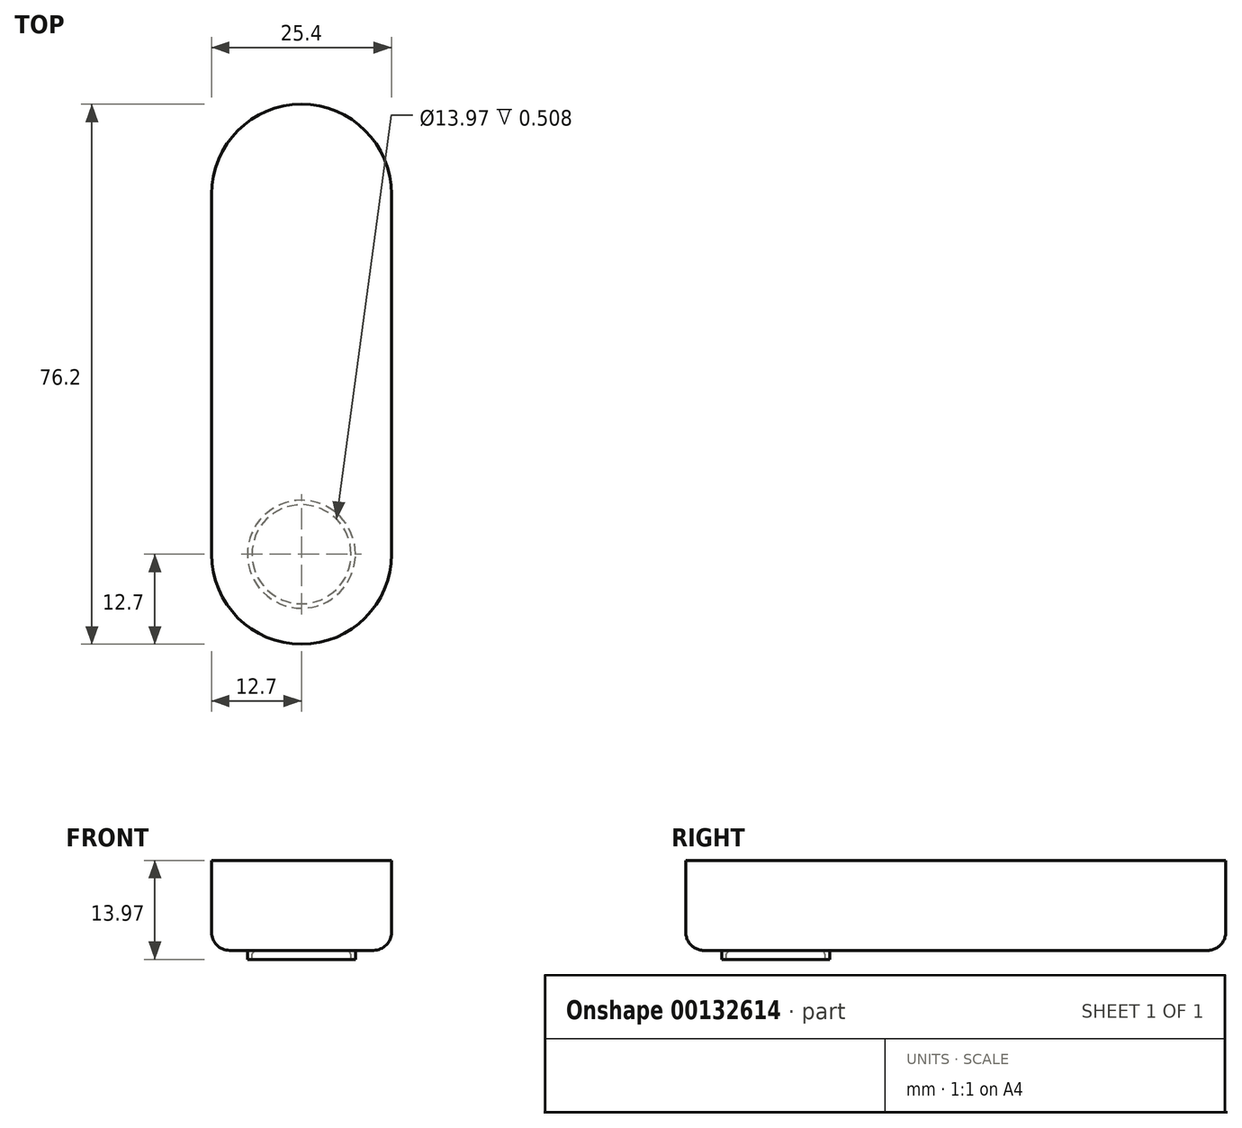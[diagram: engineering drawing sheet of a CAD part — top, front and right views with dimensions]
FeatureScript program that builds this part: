
annotation { "Feature Type Name" : "Feature", "Feature Type Description" : "" }
export const myFeature = defineFeature(function(context is Context, id is Id, definition is map)
    precondition{}
    {
        {
            var Q0;
            Q0=qCreatedBy(makeId("Top.planeOp"),FACE);
            var sketch = newSketch(context, id + "F0", { "sketchPlane" : qUnion([Q0])});
            skLineSegment(sketch, "E0.bottom", {"start": v(50.8, -50.8) * mm, "end": v(-50.8, -50.8) * mm});
            skLineSegment(sketch, "E0.top", {"start": v(50.8, 50.8) * mm, "end": v(-50.8, 50.8) * mm});
            skLineSegment(sketch, "E0.left", {"start": v(50.8, -50.8) * mm, "end": v(50.8, 50.8) * mm});
            skLineSegment(sketch, "E0.right", {"start": v(-50.8, -50.8) * mm, "end": v(-50.8, 50.8) * mm});
            skPoint(sketch, "E0.middle", {"position": v(0, 0) * mm});
            skSolve(sketch);
        }
        {
            var Q0;
            Q0=makeQuery(id+"F0.imprint","IMPRINT",FACE,{"disambiguationData":[TD([[makeQuery(id+"F0.imprint","IMPRINT",EDGE,{"derivedFrom":sQuery(id+"F0.wireOp",EDGE,"E0.bottom")}),-1.0]])]});
            extrude(context, id + "F1", {"entities" : qUnion([Q0]), "depth" : 50.8 * mm});
        }
        {
            var Q0;
            Q0=makeQuery(id+"F1.opExtrude","CAP_FACE",FACE,{"disambiguationData":[OSD([sQuery(id+"F0.wireOp",EDGE,"E0.bottom"),sQuery(id+"F0.wireOp",EDGE,"E0.top"),sQuery(id+"F0.wireOp",EDGE,"E0.left"),sQuery(id+"F0.wireOp",EDGE,"E0.right")])],"isStart":false});
            var sketch = newSketch(context, id + "F2", { "sketchPlane" : qUnion([Q0])});
            skLineSegment(sketch, "E1.bottom", {"start": v(12.7, -25.4) * mm, "end": v(-12.7, -25.4) * mm});
            skLineSegment(sketch, "E1.top", {"start": v(12.7, 25.4) * mm, "end": v(-12.7, 25.4) * mm});
            skLineSegment(sketch, "E1.left", {"start": v(12.7, -25.4) * mm, "end": v(12.7, 25.4) * mm});
            skLineSegment(sketch, "E1.right", {"start": v(-12.7, -25.4) * mm, "end": v(-12.7, 25.4) * mm});
            skPoint(sketch, "E1.middle", {"position": v(0, 0) * mm});
            skCircle(sketch, "E2", {"center": v(0, 25.4) * mm, "radius": 12.7 * mm});
            skCircle(sketch, "E3", {"center": v(0, -25.4) * mm, "radius": 12.7 * mm});
            skSolve(sketch);
        }
        {
            var Q0;
            {var subQ0=sQuery(id+"F2.wireOp",EDGE,"E1.top");Q0=makeQuery(id+"F2.imprint","IMPRINT",FACE,{"disambiguationData":[TD([[makeQuery(id+"F2.imprint","IMPRINT",EDGE,{"derivedFrom":subQ0}),-1.0]])]});}
            var Q1;
            {var subQ0=sQuery(id+"F2.wireOp",EDGE,"E1.top");Q1=makeQuery(id+"F2.imprint","IMPRINT",FACE,{"disambiguationData":[TD([[makeQuery(id+"F2.imprint","IMPRINT",EDGE,{"derivedFrom":subQ0}),1.0]])]});}
            var Q2;
            {var subQ0=sQuery(id+"F2.wireOp",EDGE,"E1.left");Q2=makeQuery(id+"F2.imprint","IMPRINT",FACE,{"disambiguationData":[TD([[makeQuery(id+"F2.imprint","IMPRINT",EDGE,{"derivedFrom":subQ0}),1.0]])]});}
            var Q3;
            {var subQ0=sQuery(id+"F2.wireOp",EDGE,"E1.bottom");Q3=makeQuery(id+"F2.imprint","IMPRINT",FACE,{"disambiguationData":[TD([[makeQuery(id+"F2.imprint","IMPRINT",EDGE,{"derivedFrom":subQ0}),-1.0]])]});}
            var Q4;
            {var subQ0=sQuery(id+"F2.wireOp",EDGE,"E1.bottom");Q4=makeQuery(id+"F2.imprint","IMPRINT",FACE,{"disambiguationData":[TD([[makeQuery(id+"F2.imprint","IMPRINT",EDGE,{"derivedFrom":subQ0}),1.0]])]});}
            extrude(context, id + "F3", {"entities" : qUnion([Q0, Q1, Q2, Q3, Q4]), "operationType" : NewBodyOperationType.REMOVE, "oppositeDirection" : true, "depth" : 12.7 * mm});
        }
        {
            var Q0;
            Q0=makeQuery(id+"F3.boolean.opBoolean","COPY",FACE,{"derivedFrom":makeQuery(id+"F3.opExtrude","CAP_FACE",FACE,{"disambiguationData":[OSD([sQuery(id+"F2.wireOp",EDGE,"E1.left"),sQuery(id+"F2.wireOp",EDGE,"E1.right"),sQuery(id+"F2.wireOp",EDGE,"E2"),sQuery(id+"F2.wireOp",EDGE,"E3")])],"isStart":false})});
            var sketch = newSketch(context, id + "F4", { "sketchPlane" : qUnion([Q0])});
            skCircle(sketch, "E4", {"center": v(0, -25.4) * mm, "radius": 7.62 * mm});
            skCircle(sketch, "E5", {"center": v(0, -25.4) * mm, "radius": 6.99 * mm});
            skSolve(sketch);
        }
        {
            var Q0;
            Q0=makeQuery(id+"F4.imprint","IMPRINT",FACE,{"disambiguationData":[TD([[makeQuery(id+"F4.imprint","IMPRINT",EDGE,{"derivedFrom":sQuery(id+"F4.wireOp",EDGE,"E4")}),1.0]])]});
            extrude(context, id + "F5", {"entities" : qUnion([Q0]), "operationType" : NewBodyOperationType.REMOVE, "oppositeDirection" : true, "depth" : 1.27 * mm});
        }
        {
            var Q0;
            Q0=makeQuery(id+"F5.boolean.opBoolean","COPY",EDGE,{"derivedFrom":makeQuery(id+"F5.opExtrude","CAP_EDGE",EDGE,{"disambiguationData":[OSD([sQuery(id+"F4.wireOp",EDGE,"E4")])],"isStart":true})});
            var Q1;
            Q1=makeQuery(id+"F1.opExtrude","CAP_EDGE",EDGE,{"disambiguationData":[OSD([sQuery(id+"F0.wireOp",EDGE,"E0.bottom")])],"isStart":true});
            chamfer(context, id + "F6", {"entities" : qUnion([Q0, Q1]), "width" : 0.76 * mm, "tangentPropagation" : true});
        }
        {
            var Q0;
            Q0=makeQuery(id+"F5.boolean.opBoolean","COPY",EDGE,{"derivedFrom":makeQuery(id+"F5.opExtrude","CAP_EDGE",EDGE,{"disambiguationData":[OSD([sQuery(id+"F4.wireOp",EDGE,"E5")])],"isStart":true})});
            fillet(context, id + "F7", {"entities" : qUnion([Q0]), "radius" : 0.76 * mm, "tangentPropagation" : true, "allowEdgeOverflow" : false});
        }
        {
            var Q0;
            Q0=makeQuery(id+"F1.opExtrude","CAP_FACE",FACE,{"disambiguationData":[OSD([sQuery(id+"F0.wireOp",EDGE,"E0.bottom"),sQuery(id+"F0.wireOp",EDGE,"E0.top"),sQuery(id+"F0.wireOp",EDGE,"E0.left"),sQuery(id+"F0.wireOp",EDGE,"E0.right")])],"isStart":false});
            var sketch = newSketch(context, id + "F8", { "sketchPlane" : qUnion([Q0])});
            skLineSegment(sketch, "E6.0", {"start": v(12.7, -25.4) * mm, "end": v(12.7, 25.4) * mm});
            skArc(sketch, "E7.0", {"start": v(12.7, 25.4) * mm, "mid": v(0, 38.1) * mm, "end": v(-12.7, 25.4) * mm});
            skLineSegment(sketch, "E8.0", {"start": v(-12.7, -25.4) * mm, "end": v(-12.7, 25.4) * mm});
            skArc(sketch, "E9.0", {"start": v(-12.7, -25.4) * mm, "mid": v(0, -38.1) * mm, "end": v(12.7, -25.4) * mm});
            skSolve(sketch);
        }
        {
            var Q0;
            Q0=makeQuery(id+"F8.imprint","IMPRINT",FACE,{"disambiguationData":[TD([[makeQuery(id+"F8.imprint","IMPRINT",EDGE,{"derivedFrom":sQuery(id+"F8.wireOp",EDGE,"E6.0")}),1.0]])]});
            extrude(context, id + "F9", {"entities" : qUnion([Q0]), "oppositeDirection" : true, "depth" : 25.4 * mm});
        }
        {
            var Q0;
            Q0=makeQuery(id+"F3.boolean.opBoolean","COPY",EDGE,{"derivedFrom":makeQuery(id+"F3.opExtrude","CAP_EDGE",EDGE,{"disambiguationData":[OSD([sQuery(id+"F2.wireOp",EDGE,"E3")])],"isStart":false})});
            fillet(context, id + "F10", {"entities" : qUnion([Q0]), "radius" : 2.54 * mm, "tangentPropagation" : true, "allowEdgeOverflow" : false});
        }
        {
            var Q0;
            Q0=makeQuery(id+"F1.opExtrude","SWEPT_BODY",BODY,{"disambiguationData":[OSD([sQuery(id+"F0.wireOp",EDGE,"E0.bottom"),sQuery(id+"F0.wireOp",EDGE,"E0.top"),sQuery(id+"F0.wireOp",EDGE,"E0.left"),sQuery(id+"F0.wireOp",EDGE,"E0.right")])]});
            var Q1;
            Q1=makeQuery(id+"F9.opExtrude","SWEPT_BODY",BODY,{"disambiguationData":[OSD([sQuery(id+"F8.wireOp",EDGE,"E6.0"),sQuery(id+"F8.wireOp",EDGE,"E7.0"),sQuery(id+"F8.wireOp",EDGE,"E8.0"),sQuery(id+"F8.wireOp",EDGE,"E9.0")])]});
            booleanBodies(context, id + "F11", {"operationType" : BooleanOperationType.SUBTRACTION, "tools" : qUnion([Q0]), "targets" : qUnion([Q1])});
        }
    });
